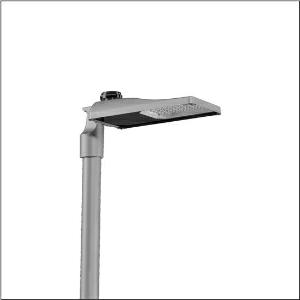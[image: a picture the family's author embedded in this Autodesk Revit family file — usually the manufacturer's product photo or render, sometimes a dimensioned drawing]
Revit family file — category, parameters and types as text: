
# Revit family: streetlight_sl_31_mini___st1_0a_5xh6d35n08ja_1cc2
name_source: partatom
category: Lighting Fixtures
units: mm (PartAtom-declared; Revit-internal decimal feet)

## family parameters
Cut with Voids When Loaded = No
Host = Face
Light Source = No
Part Type = Normal
Room Calculation Point = No
Round Connector Dimension = Use Diameter
Shared = No

## types (1)
- --- (1 x LED, 12140 lm, 81.1 W, 3000K)
    Apparent Load = 81 VA
    CIE Flux Codes = 40 73 97 100 100
    Color Rendering = 70
    Color Temperature = 3000K
    Default Elevation = 1800 mm
    Description = Streetlight SL 31 mini, mast luminaire, primary light control with lens, of PMMA, primary optical cover: cover, of toughened safety glass, transparent, light distribution: ST1.0a, light emission: direct distribution, primary light characteristic: asymmetric, installation type: post-top, side-entry, LED, High Power LED, rated luminous flux: 12.140lm, luminous efficacy: 150lm/W, light colour: 730, colour temperature: 3000K, control: presetting dimming linear, flexible luminous flux parameterisation, time-dependent luminous flux control, constant luminous flux control, intelligent temperature release in ECG and LED module, overheat protection, with cable H07RN-F 3x 1.5mm², mains connection: 220..240V, AC, 50/60Hz, connection cable pre-assembled, cable length: 10,5m, start of lifetime: 81W, end of service life: 88W, reduction: 36W, luminaire housing, of diecast aluminium, powder-coated, Siteco® metallic grey (DB 702S), corrosivity category C5 high according to DIN EN ISO 12944, no sealing on luminaire upper side, inclination: -15°..+20° (post-top) | -20°..+20° (side-entry), adjustable in 5° steps, mast flange (76/60mm) included as standard, multi-level sealing system, sealing non-destructively replaceable, protection rating (complete): IP66, insulation class (complete): insulation class I (protective earthing), certification: CE, ENEC, ENEC+, VDE, UKCA, impact resistance: IK09, permissible operating ambient temperature for outdoor applications: -40..+50°C, standard-compliant lighting for roads and squares, packaging unit: 1 piece

Light Distribution: ST1.0a
    Height = 76 mm
    Lamp = 1 x LED
    Lamp Light Flux = 12140 lm
    Lamp Power = 81.1 W
    Lamp count = 1
    Length = 547 mm
    Luminous efficacy = 150 lm/W
    Manufacturer = Siteco
    ModVariant = No
    Model = 5XH6D35N08JA
    Number of Poles = 1
    OnlyDefault = Yes
    Power Factor = 1
    Product Name = Streetlight SL 31 mini | ST1.0a
    Product group = mast luminaire | pylon top
    ProductGroupID = 6100
    Protection Class = Protection class I
    Protection Degree = IP 66
    RLX_Detail_Level = 1
    RLX_Emergency_Light_Flux = 0 lm
    RLX_Emergency_Type = 0
    RLX_Emergency_Type_DB = No
    RlxData = <blob elided: 40505 chars, md5=2f2c56ce>
    Socket = socket
    Standby Power = 0 W
    System Light Flux = 12140 lm
    System Power = 81 W
    Type Comments = factory setting: luminous flux: 100 % | dim-lin: 254 | 860 mA
    Type Image = l_1300322.jpg
    URL = http://relux.com
    VarID = @adj_007735
    Voltage = 0 V
    Weight = 0.00 kg
    Width = 265 mm

## geometry (parser evidence)
native form markers: Blend x4, Sweep x11
no freeform markers — native parametric forms only
